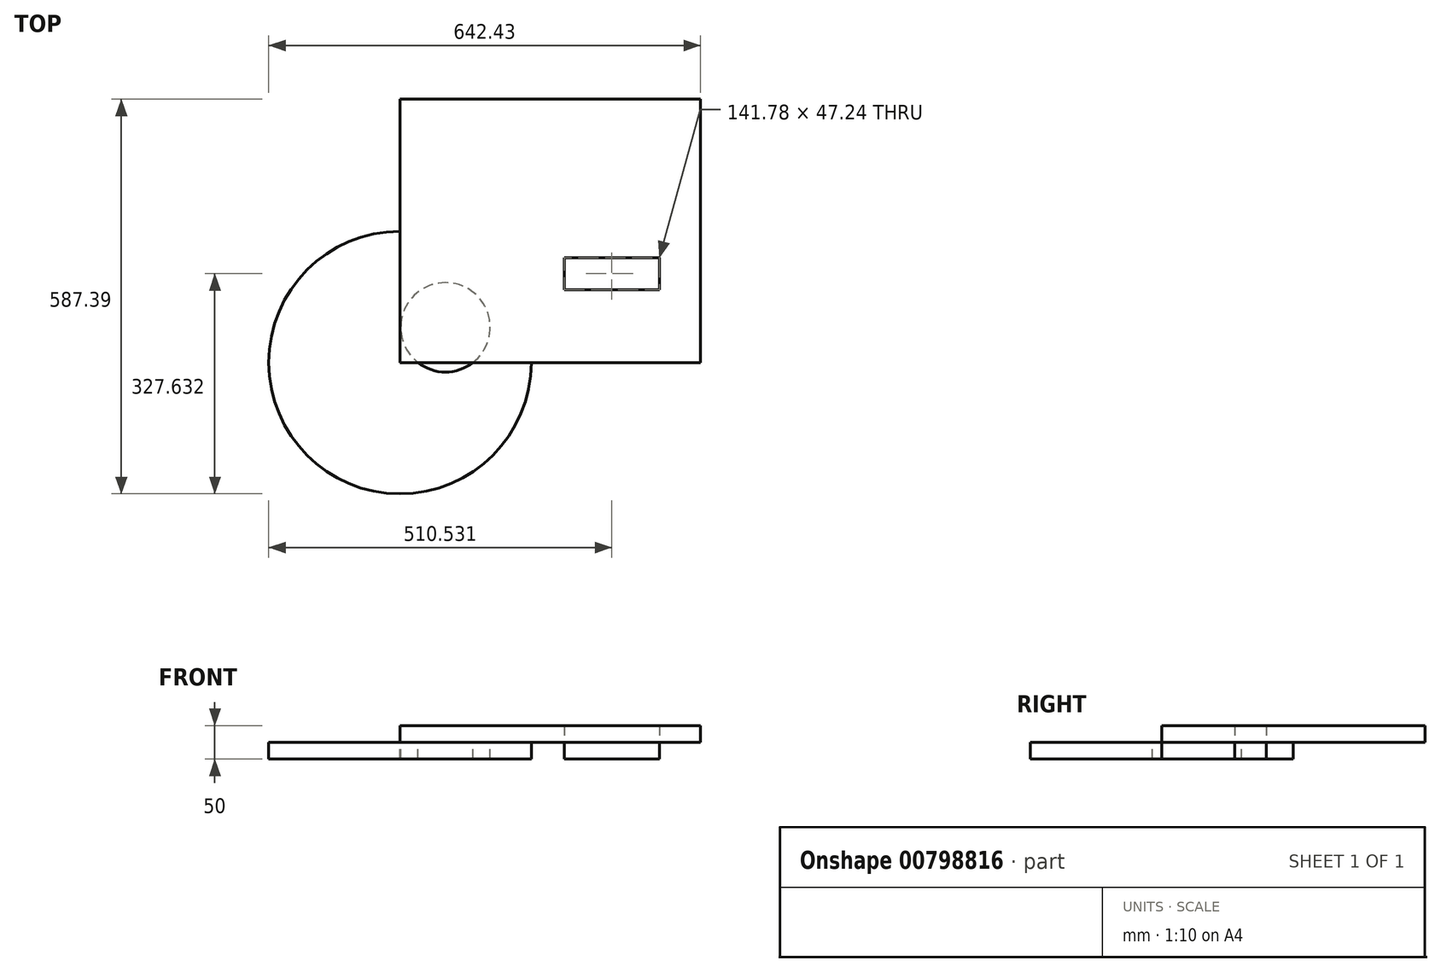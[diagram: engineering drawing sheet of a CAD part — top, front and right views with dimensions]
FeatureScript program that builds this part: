
annotation { "Feature Type Name" : "Feature", "Feature Type Description" : "" }
export const myFeature = defineFeature(function(context is Context, id is Id, definition is map)
    precondition{}
    {
        {
            var Q0;
            Q0=qCreatedBy(makeId("Top.planeOp"),FACE);
            var sketch = newSketch(context, id + "F0", { "sketchPlane" : qUnion([Q0])});
            skLineSegment(sketch, "E0.bottom", {"start": v(0, -47.24) * mm, "end": v(141.78, -47.24) * mm});
            skLineSegment(sketch, "E0.top", {"start": v(0, 0) * mm, "end": v(141.78, 0) * mm});
            skLineSegment(sketch, "E0.left", {"start": v(0, -47.24) * mm, "end": v(0, 0) * mm});
            skLineSegment(sketch, "E0.right", {"start": v(141.78, -47.24) * mm, "end": v(141.78, 0) * mm});
            skSolve(sketch);
        }
        {
            var Q0;
            Q0=makeQuery(id+"F0.imprint","IMPRINT",FACE,{"disambiguationData":[TD([[makeQuery(id+"F0.imprint","IMPRINT",EDGE,{"derivedFrom":sQuery(id+"F0.wireOp",EDGE,"E0.bottom")}),1.0]])]});
            var sketch = newSketch(context, id + "F1", { "sketchPlane" : qUnion([Q0])});
            skSolve(sketch);
        }
        {
            var Q0;
            Q0=makeQuery(id+"F0.imprint","IMPRINT",FACE,{"disambiguationData":[TD([[makeQuery(id+"F0.imprint","IMPRINT",EDGE,{"derivedFrom":sQuery(id+"F0.wireOp",EDGE,"E0.bottom")}),1.0]])]});
            extrude(context, id + "F2", {"entities" : qUnion([Q0]), "depth" : 25 * mm, "offsetDistance" : 25 * mm});
        }
        {
            var Q0;
            Q0=makeQuery(id+"F1.imprint","IMPRINT",FACE,{"disambiguationData":[TD([[makeQuery(id+"F1.imprint","IMPRINT",EDGE,{"derivedFrom":makeQuery(id+"F0.imprint","IMPRINT",EDGE,{"derivedFrom":sQuery(id+"F0.wireOp",EDGE,"E0.bottom")})}),1.0]])]});
            extrude(context, id + "F3", {"entities" : qUnion([Q0]), "depth" : 25 * mm, "offsetDistance" : 25 * mm});
        }
        {
            var Q0;
            Q0=makeQuery(id+"F2.opExtrude","CAP_FACE",FACE,{"disambiguationData":[OSD([sQuery(id+"F0.wireOp",EDGE,"E0.bottom"),sQuery(id+"F0.wireOp",EDGE,"E0.top"),sQuery(id+"F0.wireOp",EDGE,"E0.left"),sQuery(id+"F0.wireOp",EDGE,"E0.right")])],"isStart":false});
            var sketch = newSketch(context, id + "F4", { "sketchPlane" : qUnion([Q0])});
            skLineSegment(sketch, "E1.bottom", {"start": v(202.79, -155.9) * mm, "end": v(-244.28, -155.9) * mm});
            skLineSegment(sketch, "E1.top", {"start": v(202.79, 236.14) * mm, "end": v(-244.28, 236.14) * mm});
            skLineSegment(sketch, "E1.left", {"start": v(202.79, -155.9) * mm, "end": v(202.79, 236.14) * mm});
            skLineSegment(sketch, "E1.right", {"start": v(-244.28, -155.9) * mm, "end": v(-244.28, 236.14) * mm});
            skPoint(sketch, "E1.middle", {"position": v(-20.75, 40.12) * mm});
            skSolve(sketch);
        }
        {
            var Q0;
            Q0=makeQuery(id+"F4.imprint","IMPRINT",FACE,{"disambiguationData":[TD([[makeQuery(id+"F4.imprint","IMPRINT",EDGE,{"derivedFrom":sQuery(id+"F4.wireOp",EDGE,"E1.bottom")}),-1.0]])]});
            extrude(context, id + "F5", {"entities" : qUnion([Q0]), "depth" : 25 * mm, "offsetDistance" : 25 * mm});
        }
        {
            var Q0;
            Q0=makeQuery(id+"F5.opExtrude","CAP_FACE",FACE,{"disambiguationData":[OSD([sQuery(id+"F0.wireOp",EDGE,"E0.bottom"),sQuery(id+"F0.wireOp",EDGE,"E0.top"),sQuery(id+"F0.wireOp",EDGE,"E0.left"),sQuery(id+"F0.wireOp",EDGE,"E0.right"),sQuery(id+"F4.wireOp",EDGE,"E1.bottom"),sQuery(id+"F4.wireOp",EDGE,"E1.top"),sQuery(id+"F4.wireOp",EDGE,"E1.left"),sQuery(id+"F4.wireOp",EDGE,"E1.right")])],"isStart":true});
            var sketch = newSketch(context, id + "F6", { "sketchPlane" : qUnion([Q0])});
            skCircle(sketch, "E2", {"center": v(-244.28, 155.9) * mm, "radius": 195.35 * mm});
            skCircle(sketch, "E3", {"center": v(-324.42, 163.02) * mm, "radius": 58.2 * mm});
            skCircle(sketch, "E4", {"center": v(-176.7, 103.42) * mm, "radius": 66.56 * mm});
            skSolve(sketch);
        }
        {
            var Q0;
            Q0=makeQuery(id+"F6.imprint","IMPRINT",FACE,{"disambiguationData":[TD([[makeQuery(id+"F6.imprint","IMPRINT",EDGE,{"derivedFrom":sQuery(id+"F6.wireOp",EDGE,"E3")}),-1.0]])]});
            var Q1;
            {var subQ0=sQuery(id+"F6.wireOp",EDGE,"E4");var subQ1=makeQuery(id+"F5.opExtrude","CAP_EDGE",EDGE,{"disambiguationData":[OSD([sQuery(id+"F4.wireOp",EDGE,"E1.bottom")])],"isStart":true});var subQ2=makeQuery(id+"F6.imprint","INTERSECT",VERTEX,{"disambiguationData":[OD(0.0)],"derivedFrom":[subQ1,subQ0]});Q1=makeQuery(id+"F6.imprint","IMPRINT",FACE,{"disambiguationData":[TD([[makeQuery(id+"F6.imprint","IMPRINT",EDGE,{"disambiguationData":[TD([[subQ2,-1.0]])],"derivedFrom":subQ0}),1.0]])]});}
            var Q2;
            Q2=makeQuery(id+"F6.imprint","IMPRINT",FACE,{"disambiguationData":[TD([[makeQuery(id+"F6.imprint","IMPRINT",EDGE,{"derivedFrom":sQuery(id+"F6.wireOp",EDGE,"E3")}),1.0]])]});
            extrude(context, id + "F7", {"entities" : qUnion([Q0, Q1, Q2]), "operationType" : NewBodyOperationType.ADD, "depth" : 25 * mm, "offsetDistance" : 25 * mm});
        }
    });
